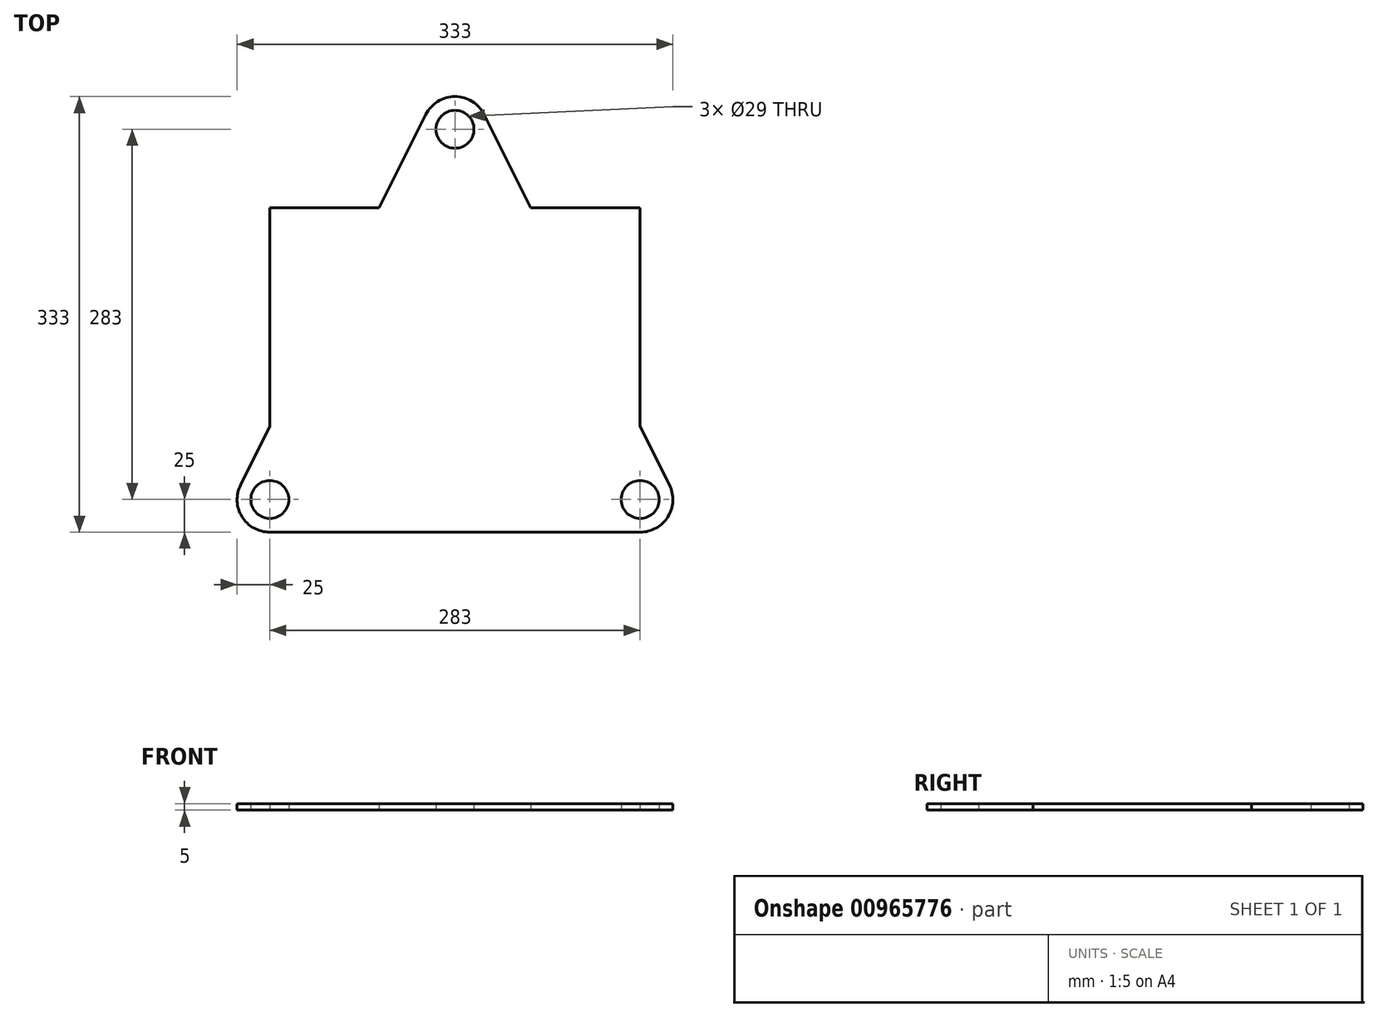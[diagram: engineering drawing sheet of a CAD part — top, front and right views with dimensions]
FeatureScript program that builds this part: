
annotation { "Feature Type Name" : "Feature", "Feature Type Description" : "" }
export const myFeature = defineFeature(function(context is Context, id is Id, definition is map)
    precondition{}
    {
        {
            var Q0;
            Q0=qCreatedBy(makeId("Top.planeOp"),FACE);
            var sketch = newSketch(context, id + "F0", { "sketchPlane" : qUnion([Q0])});
            skLineSegment(sketch, "E0.bottom", {"start": v(141.5, -100) * mm, "end": v(-141.5, -100) * mm, "construction": true});
            skPoint(sketch, "E0.middle", {"position": v(0, 0) * mm});
            skLineSegment(sketch, "E1", {"start": v(-141.5, -100) * mm, "end": v(0, 183) * mm, "construction": true});
            skPoint(sketch, "E1.endSnap0", {"position": v(0, -100) * mm});
            skLineSegment(sketch, "E2", {"start": v(0, 183) * mm, "end": v(141.5, -100) * mm, "construction": true});
            skCircle(sketch, "E3", {"center": v(-141.5, -100) * mm, "radius": 14.5 * mm});
            skCircle(sketch, "E4", {"center": v(141.5, -100) * mm, "radius": 14.5 * mm});
            skCircle(sketch, "E5", {"center": v(0, 183) * mm, "radius": 14.5 * mm});
            skArc(sketch, "E6", {"start": v(-163.86, -88.82) * mm, "mid": v(-162.77, -113.14) * mm, "end": v(-141.5, -125) * mm});
            skArc(sketch, "E7", {"start": v(141.5, -125) * mm, "mid": v(162.77, -113.14) * mm, "end": v(163.86, -88.82) * mm});
            skArc(sketch, "E8", {"start": v(22.36, 194.18) * mm, "mid": v(0, 208) * mm, "end": v(-22.36, 194.18) * mm});
            skLineSegment(sketch, "E9", {"start": v(-141.5, -125) * mm, "end": v(141.5, -125) * mm});
            skLineSegment(sketch, "E10", {"start": v(163.86, -88.82) * mm, "end": v(22.36, 194.18) * mm});
            skLineSegment(sketch, "E11", {"start": v(-22.36, 194.18) * mm, "end": v(-163.86, -88.82) * mm});
            skLineSegment(sketch, "E12.bottom", {"start": v(-141.5, 123) * mm, "end": v(141.5, 123) * mm});
            skLineSegment(sketch, "E12.top", {"start": v(-141.5, -49.66) * mm, "end": v(141.5, -49.66) * mm});
            skLineSegment(sketch, "E12.left", {"start": v(-141.5, 123) * mm, "end": v(-141.5, -49.66) * mm});
            skLineSegment(sketch, "E12.right", {"start": v(141.5, 123) * mm, "end": v(141.5, -49.66) * mm});
            skLineSegment(sketch, "E13", {"start": v(-151.38, 203) * mm, "end": v(149.67, 203) * mm, "construction": true});
            skSolve(sketch);
        }
        {
            var Q0;
            Q0 = qSketchRegion(id + "F0", true);
            extrude(context, id + "F1", {"entities" : qUnion([Q0]), "depth" : 5 * mm, "offsetDistance" : 25 * mm});
        }
    });
